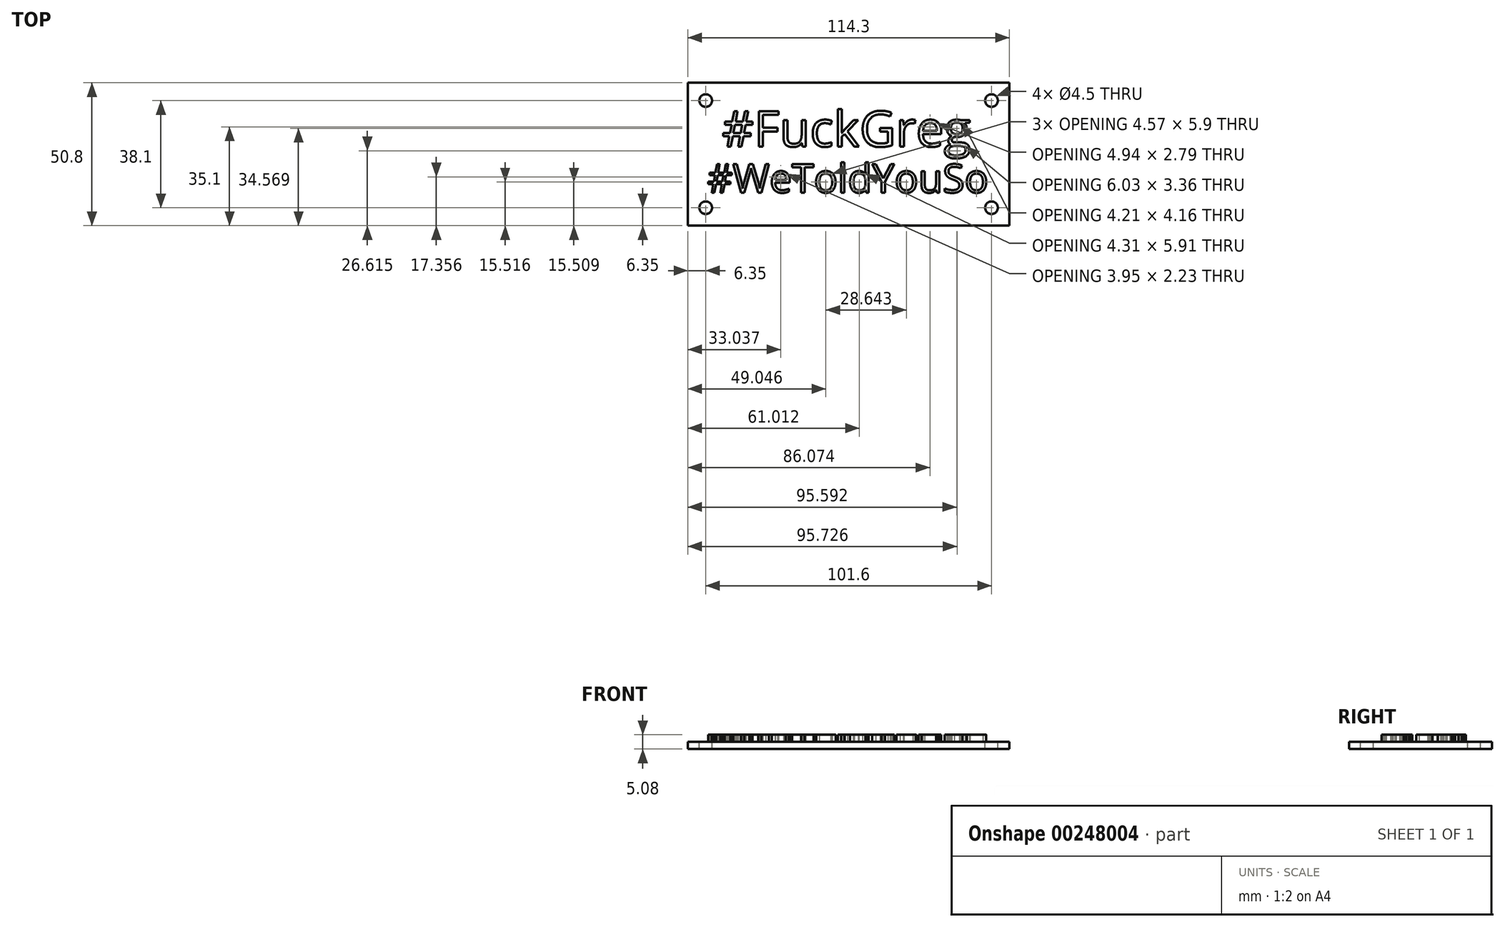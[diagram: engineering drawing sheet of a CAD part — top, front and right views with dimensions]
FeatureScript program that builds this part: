
annotation { "Feature Type Name" : "Feature", "Feature Type Description" : "" }
export const myFeature = defineFeature(function(context is Context, id is Id, definition is map)
    precondition{}
    {
        {
            var Q0;
            Q0=qCreatedBy(makeId("Top.planeOp"),FACE);
            var sketch = newSketch(context, id + "F0", { "sketchPlane" : qUnion([Q0])});
            skText(sketch, "E0", { "text": "#FuckGreg", "fontName": "OpenSans-Regular.ttf"});
            skText(sketch, "E1", { "text": "#WeToldYouSo", "fontName": "OpenSans-Regular.ttf"});
            const initialGuessF0  = {"E0": [-0.10222, 0.02808, 1, 0, 0.0127], "E1": [-0.10742, 0.01174, 1, 0, 0.01016]};
            skSetInitialGuess(sketch, initialGuessF0);
            skSolve(sketch);
        }
        {
            var Q0;
            Q0=qCreatedBy(makeId("Top.planeOp"),FACE);
            var sketch = newSketch(context, id + "F1", { "sketchPlane" : qUnion([Q0])});
            skLineSegment(sketch, "E2.bottom", {"start": v(0, 0) * mm, "end": v(-114.3, 0) * mm});
            skLineSegment(sketch, "E2.top", {"start": v(0, 50.8) * mm, "end": v(-114.3, 50.8) * mm});
            skLineSegment(sketch, "E2.left", {"start": v(0, 0) * mm, "end": v(0, 50.8) * mm});
            skLineSegment(sketch, "E2.right", {"start": v(-114.3, 0) * mm, "end": v(-114.3, 50.8) * mm});
            skSolve(sketch);
        }
        {
            var Q0;
            Q0 = qSketchRegion(id + "F1", true);
            extrude(context, id + "F2", {"entities" : qUnion([Q0]), "oppositeDirection" : true, "depth" : 2.54 * mm});
        }
        {
            var Q0;
            Q0 = qSketchRegion(id + "F0", true);
            extrude(context, id + "F3", {"entities" : qUnion([Q0]), "depth" : 2.54 * mm});
        }
        {
            var Q0;
            Q0=makeQuery(id+"F2.opExtrude","CAP_FACE",FACE,{"disambiguationData":[OSD([sQuery(id+"F1.wireOp",EDGE,"E2.bottom"),sQuery(id+"F1.wireOp",EDGE,"E2.top"),sQuery(id+"F1.wireOp",EDGE,"E2.left"),sQuery(id+"F1.wireOp",EDGE,"E2.right")])],"isStart":true});
            var sketch = newSketch(context, id + "F4", { "sketchPlane" : qUnion([Q0])});
            skCircle(sketch, "E3", {"center": v(-107.95, 44.45) * mm, "radius": 2.25 * mm});
            skCircle(sketch, "E4", {"center": v(-6.35, 44.45) * mm, "radius": 2.25 * mm});
            skCircle(sketch, "E5", {"center": v(-6.35, 6.35) * mm, "radius": 2.25 * mm});
            skCircle(sketch, "E6", {"center": v(-107.95, 6.35) * mm, "radius": 2.25 * mm});
            skSolve(sketch);
        }
        {
            var Q0;
            Q0 = qSketchRegion(id + "F4", true);
            extrude(context, id + "F5", {"entities" : qUnion([Q0]), "operationType" : NewBodyOperationType.REMOVE, "endBound" : BoundingType.THROUGH_ALL, "oppositeDirection" : true, "depth" : 25.4 * mm});
        }
    });
